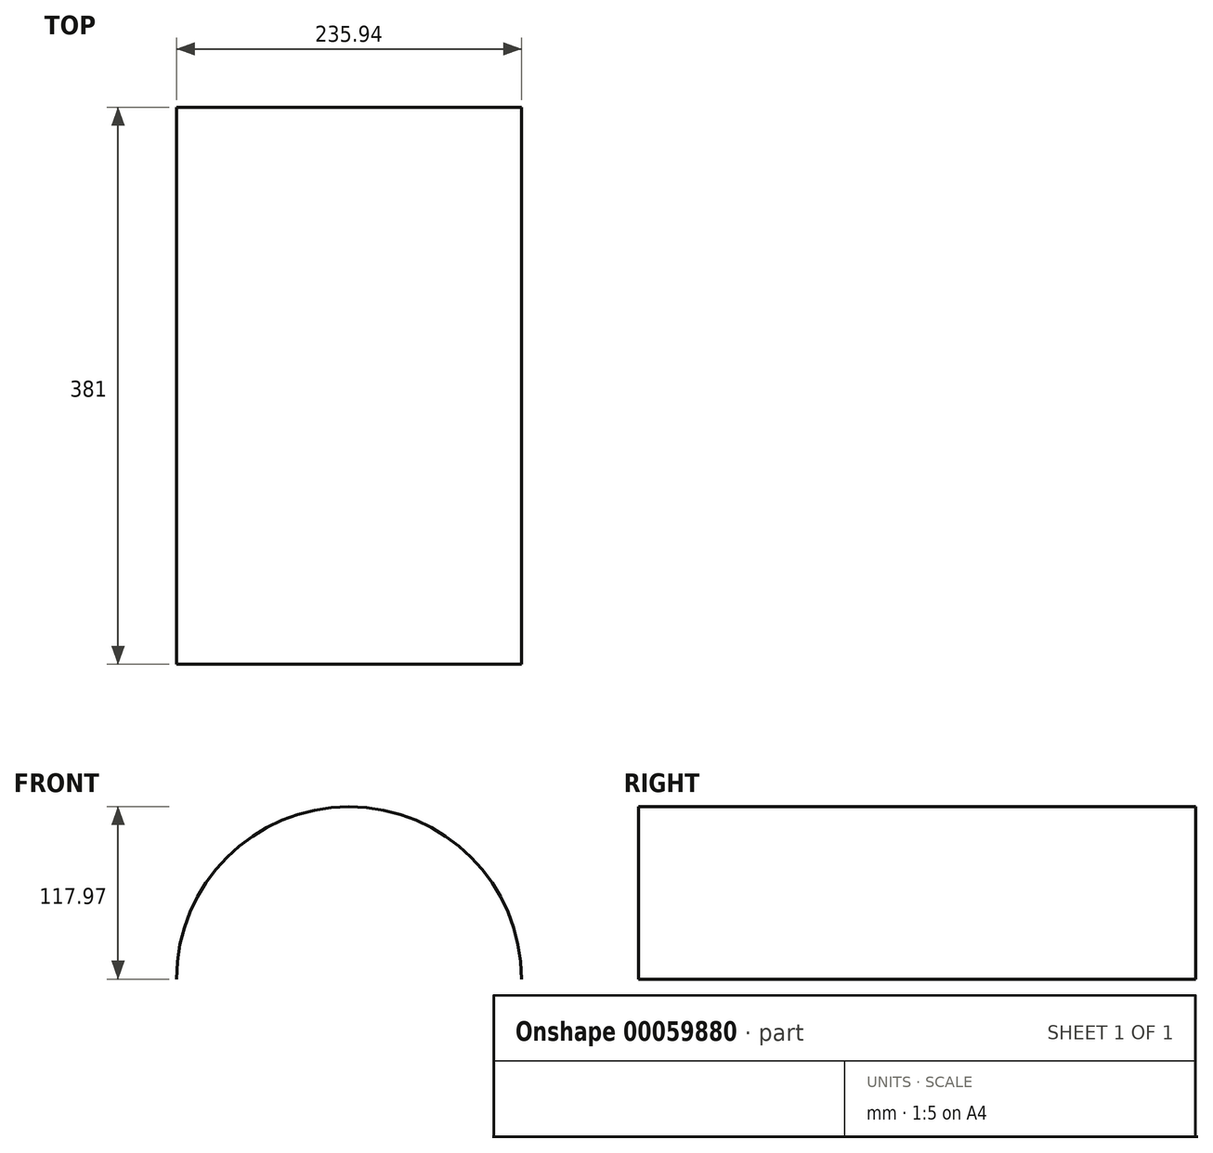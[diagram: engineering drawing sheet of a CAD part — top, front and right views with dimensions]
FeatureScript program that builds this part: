
annotation { "Feature Type Name" : "Feature", "Feature Type Description" : "" }
export const myFeature = defineFeature(function(context is Context, id is Id, definition is map)
    precondition{}
    {
        {
            var Q0;
            Q0=qCreatedBy(makeId("Front.planeOp"),FACE);
            var sketch = newSketch(context, id + "F0", { "sketchPlane" : qUnion([Q0])});
            skArc(sketch, "E0", {"start": v(117.97, 0) * mm, "mid": v(0, 117.97) * mm, "end": v(-117.97, 0) * mm});
            skLineSegment(sketch, "E1", {"start": v(-238.82, 0) * mm, "end": v(142.18, 0) * mm, "construction": true});
            skSolve(sketch);
        }
        {
            var Q0;
            Q0=sQuery(id+"F0.wireOp",EDGE,"E0");
            extrude(context, id + "F1", {"bodyType" : ToolBodyType.SURFACE, "surfaceEntities" : qUnion([Q0]), "depth" : 381 * mm});
        }
    });
